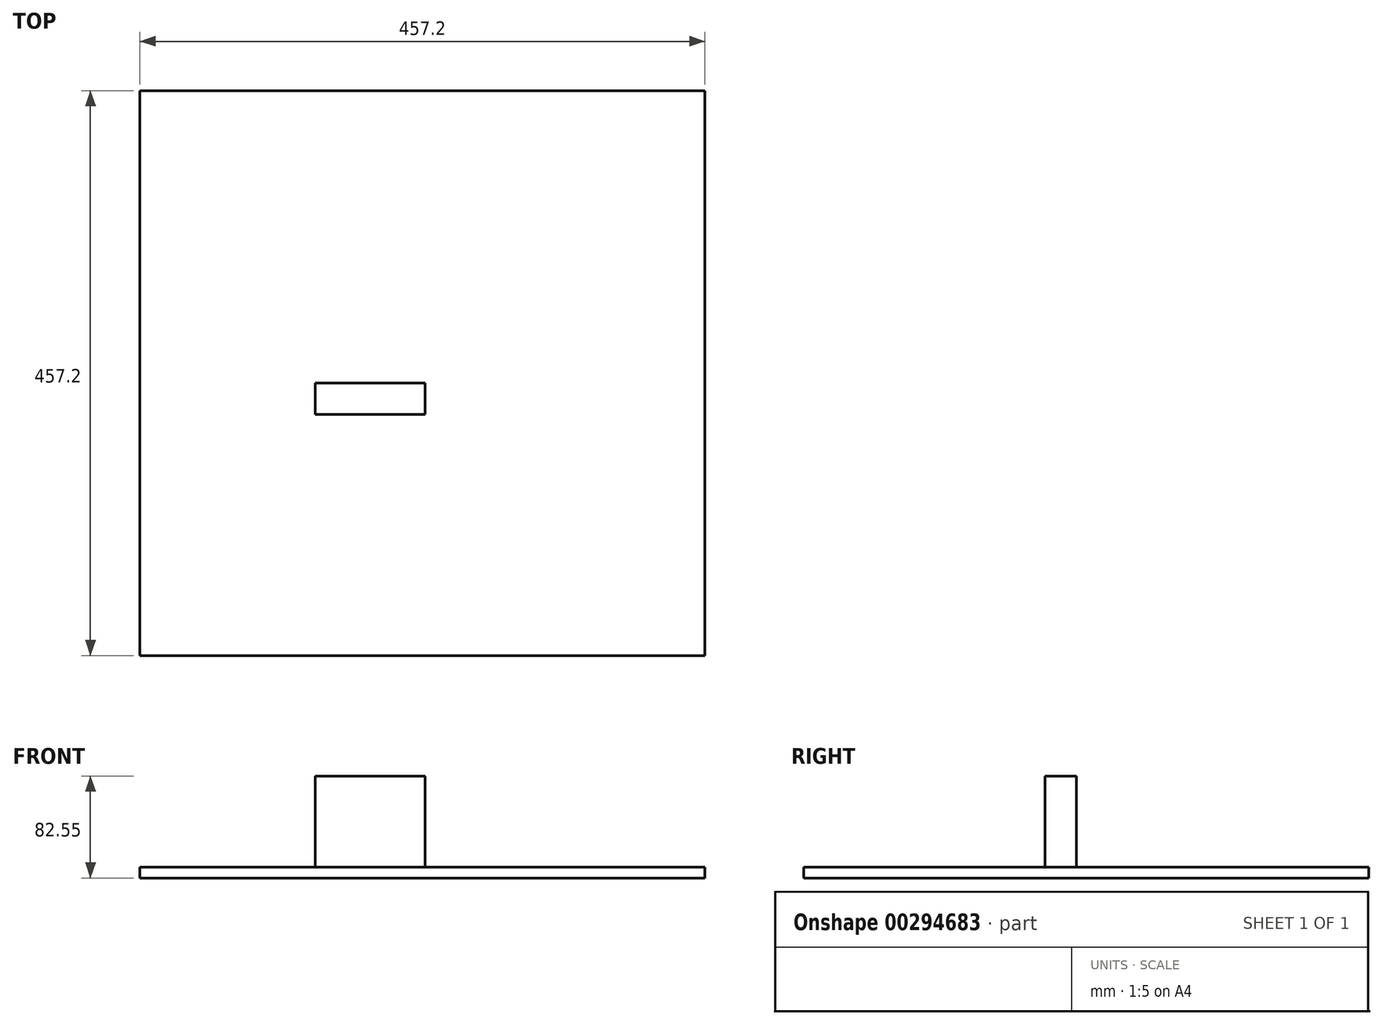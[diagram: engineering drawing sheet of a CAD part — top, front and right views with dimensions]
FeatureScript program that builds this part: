
annotation { "Feature Type Name" : "Feature", "Feature Type Description" : "" }
export const myFeature = defineFeature(function(context is Context, id is Id, definition is map)
    precondition{}
    {
        {
            var Q0;
            Q0=qCreatedBy(makeId("Top.planeOp"),FACE);
            var sketch = newSketch(context, id + "F0", { "sketchPlane" : qUnion([Q0])});
            skLineSegment(sketch, "E0", {"start": v(-230.87, 236.56) * mm, "end": v(-230.87, -220.64) * mm});
            skLineSegment(sketch, "E1", {"start": v(-230.87, -220.64) * mm, "end": v(226.33, -220.64) * mm});
            skLineSegment(sketch, "E2", {"start": v(226.33, -220.64) * mm, "end": v(226.33, 236.56) * mm});
            skLineSegment(sketch, "E3", {"start": v(226.33, 236.56) * mm, "end": v(-230.87, 236.56) * mm});
            skSolve(sketch);
        }
        {
            var Q0;
            Q0=makeQuery(id+"F0.imprint","IMPRINT",FACE,{"disambiguationData":[TD([[makeQuery(id+"F0.imprint","IMPRINT",EDGE,{"derivedFrom":sQuery(id+"F0.wireOp",EDGE,"E0")}),1.0]])]});
            extrude(context, id + "F1", {"entities" : qUnion([Q0]), "depth" : 8.64 * mm});
        }
        {
            var Q0;
            Q0=qCreatedBy(makeId("Front.planeOp"),FACE);
            var sketch = newSketch(context, id + "F2", { "sketchPlane" : qUnion([Q0])});
            skLineSegment(sketch, "E4.bottom", {"start": v(0, 0) * mm, "end": v(-88.9, 0) * mm});
            skLineSegment(sketch, "E4.top", {"start": v(0, 82.55) * mm, "end": v(-88.9, 82.55) * mm});
            skLineSegment(sketch, "E4.left", {"start": v(0, 0) * mm, "end": v(0, 82.55) * mm});
            skLineSegment(sketch, "E4.right", {"start": v(-88.9, 0) * mm, "end": v(-88.9, 82.55) * mm});
            skLineSegment(sketch, "E5.0.0", {"start": v(226.33, 8.64) * mm, "end": v(226.33, 8.64) * mm});
            skLineSegment(sketch, "E5.0.1", {"start": v(226.33, 8.64) * mm, "end": v(-230.87, 8.64) * mm});
            skLineSegment(sketch, "E5.0.2", {"start": v(-230.87, 8.64) * mm, "end": v(-230.87, 8.64) * mm});
            skLineSegment(sketch, "E5.0.3", {"start": v(-230.87, 8.64) * mm, "end": v(226.33, 8.64) * mm});
            skSolve(sketch);
        }
        {
            var Q0;
            Q0 = qSketchRegion(id + "F2", true);
            extrude(context, id + "F3", {"entities" : qUnion([Q0]), "operationType" : NewBodyOperationType.ADD, "depth" : 25.4 * mm});
        }
    });
